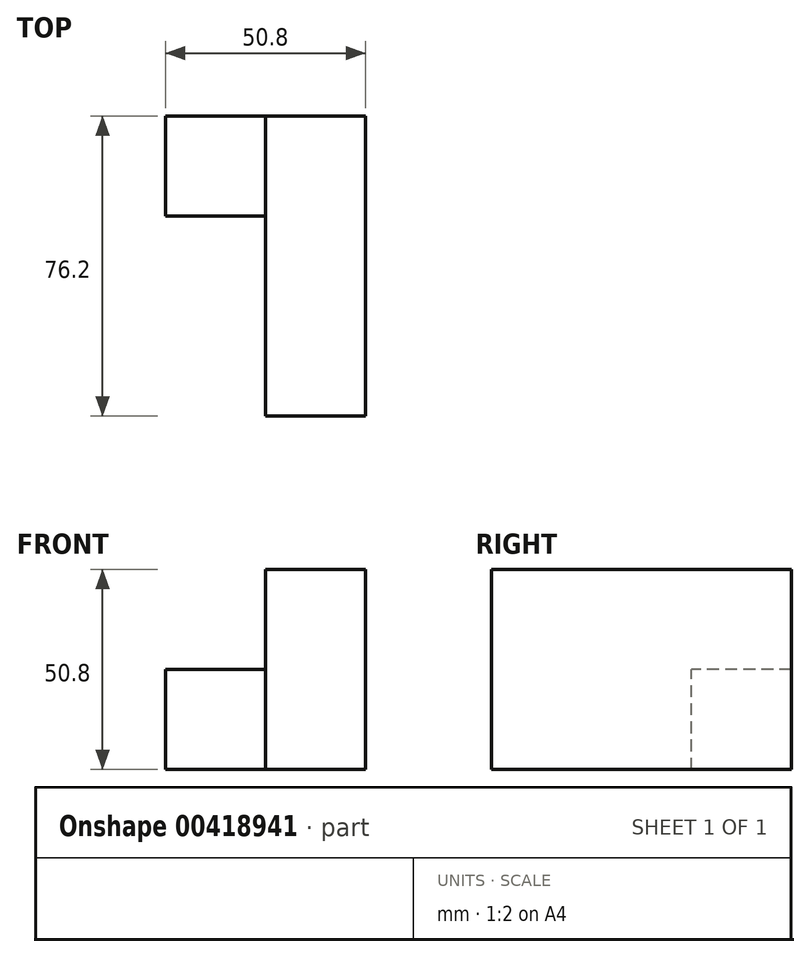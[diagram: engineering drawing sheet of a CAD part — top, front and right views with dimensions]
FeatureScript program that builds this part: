
annotation { "Feature Type Name" : "Feature", "Feature Type Description" : "" }
export const myFeature = defineFeature(function(context is Context, id is Id, definition is map)
    precondition{}
    {
        {
            var Q0;
            Q0=qCreatedBy(makeId("Front.planeOp"),FACE);
            var sketch = newSketch(context, id + "F0", { "sketchPlane" : qUnion([Q0])});
            skLineSegment(sketch, "E0.bottom", {"start": v(-75.8, 55.96) * mm, "end": v(-50.4, 55.96) * mm});
            skLineSegment(sketch, "E0.top", {"start": v(-75.8, 5.16) * mm, "end": v(-50.4, 5.16) * mm});
            skLineSegment(sketch, "E0.left", {"start": v(-75.8, 55.96) * mm, "end": v(-75.8, 5.16) * mm});
            skLineSegment(sketch, "E0.right", {"start": v(-50.4, 55.96) * mm, "end": v(-50.4, 5.16) * mm});
            skSolve(sketch);
        }
        {
            var Q0;
            Q0 = qSketchRegion(id + "F0", true);
            extrude(context, id + "F1", {"entities" : qUnion([Q0]), "depth" : 50.8 * mm});
        }
        {
            var Q0;
            Q0=makeQuery(id+"F1.opExtrude","CAP_FACE",FACE,{"disambiguationData":[OSD([sQuery(id+"F0.wireOp",EDGE,"E0.bottom"),sQuery(id+"F0.wireOp",EDGE,"E0.top"),sQuery(id+"F0.wireOp",EDGE,"E0.left"),sQuery(id+"F0.wireOp",EDGE,"E0.right")])],"isStart":false});
            var sketch = newSketch(context, id + "F2", { "sketchPlane" : qUnion([Q0])});
            skSolve(sketch);
        }
        {
            var Q0;
            Q0 = qSketchRegion(id + "F2", true);
            var Q1;
            Q1=makeQuery(id+"F2.imprint","IMPRINT",FACE,{"disambiguationData":[TD([[makeQuery(id+"F2.imprint","IMPRINT",EDGE,{"derivedFrom":makeQuery(id+"F1.opExtrude","CAP_EDGE",EDGE,{"disambiguationData":[OSD([sQuery(id+"F0.wireOp",EDGE,"E0.bottom")])],"isStart":false})}),-1.0]])]});
            extrude(context, id + "F3", {"entities" : qUnion([Q0, Q1]), "operationType" : NewBodyOperationType.ADD, "depth" : 25.4 * mm});
        }
        {
            var Q0;
            {var subQ0=sQuery(id+"F0.wireOp",EDGE,"E0.left");Q0=makeQuery(id+"F3.boolean.opBoolean","MERGE",FACE,{"derivedFrom":[makeQuery(id+"F1.opExtrude","SWEPT_FACE",FACE,{"disambiguationData":[OSD([subQ0])]}),makeQuery(id+"F3.opExtrude","SWEPT_FACE",FACE,{"disambiguationData":[OSD([subQ0])]})]});}
            var sketch = newSketch(context, id + "F4", { "sketchPlane" : qUnion([Q0])});
            skLineSegment(sketch, "E1.bottom", {"start": v(0, 5.16) * mm, "end": v(25.4, 5.16) * mm});
            skLineSegment(sketch, "E1.top", {"start": v(0, 30.56) * mm, "end": v(25.4, 30.56) * mm});
            skLineSegment(sketch, "E1.left", {"start": v(0, 5.16) * mm, "end": v(0, 30.56) * mm});
            skLineSegment(sketch, "E1.right", {"start": v(25.4, 5.16) * mm, "end": v(25.4, 30.56) * mm});
            skSolve(sketch);
        }
        {
            var Q0;
            Q0 = qSketchRegion(id + "F4", true);
            extrude(context, id + "F5", {"entities" : qUnion([Q0]), "operationType" : NewBodyOperationType.ADD, "depth" : 25.4 * mm});
        }
    });
